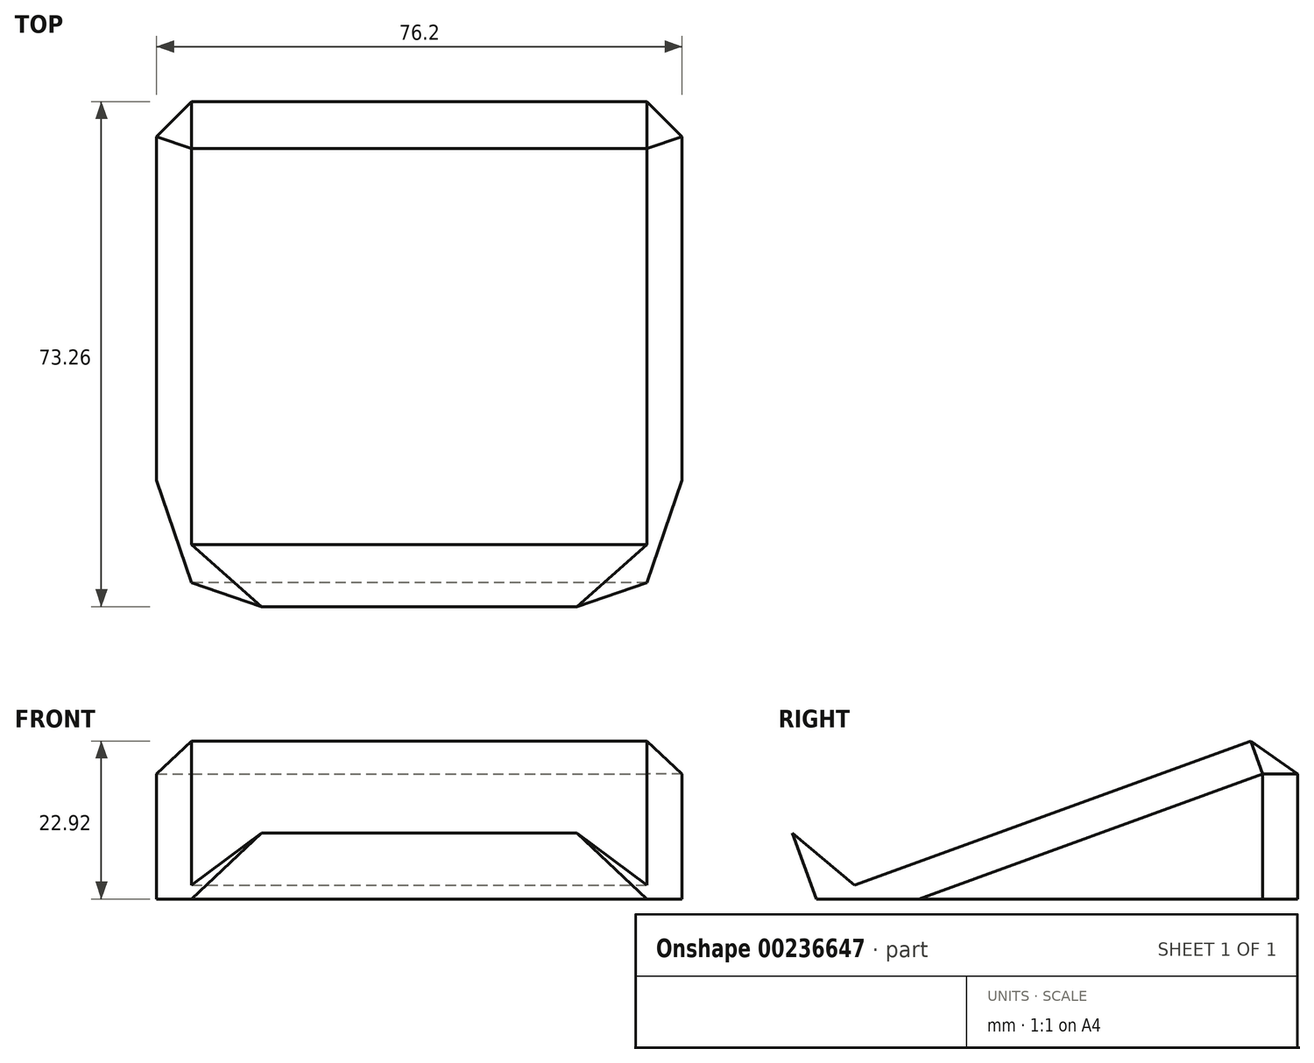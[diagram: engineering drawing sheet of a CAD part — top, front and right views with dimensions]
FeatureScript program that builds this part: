
annotation { "Feature Type Name" : "Feature", "Feature Type Description" : "" }
export const myFeature = defineFeature(function(context is Context, id is Id, definition is map)
    precondition{}
    {
        {
            var Q0;
            Q0=qCreatedBy(makeId("Right.planeOp"),FACE);
            var sketch = newSketch(context, id + "F0", { "sketchPlane" : qUnion([Q0])});
            skLineSegment(sketch, "E0", {"start": v(0, 0) * mm, "end": v(0, 25.4) * mm});
            skLineSegment(sketch, "E1", {"start": v(0, 0) * mm, "end": v(-69.79, 0) * mm});
            skLineSegment(sketch, "E2", {"start": v(-69.79, 0) * mm, "end": v(0, 25.4) * mm});
            skSolve(sketch);
        }
        {
            var Q0;
            Q0 = qSketchRegion(id + "F0", true);
            extrude(context, id + "F1", {"entities" : qUnion([Q0]), "depth" : 76.2 * mm});
        }
        {
            var Q0;
            Q0=makeQuery(id+"F1.opExtrude","CAP_EDGE",EDGE,{"disambiguationData":[OSD([sQuery(id+"F0.wireOp",EDGE,"E2")])],"isStart":true});
            var Q1;
            Q1=makeQuery(id+"F1.opExtrude","CAP_EDGE",EDGE,{"disambiguationData":[OSD([sQuery(id+"F0.wireOp",EDGE,"E0")])],"isStart":true});
            var Q2;
            Q2=makeQuery(id+"F1.opExtrude","SWEPT_EDGE",EDGE,{"disambiguationData":[OSD([sQuery(id+"F0.wireOp",EDGE,"E0"),sQuery(id+"F0.wireOp",EDGE,"E2")])]});
            var Q3;
            Q3=makeQuery(id+"F1.opExtrude","CAP_EDGE",EDGE,{"disambiguationData":[OSD([sQuery(id+"F0.wireOp",EDGE,"E2")])],"isStart":false});
            var Q4;
            Q4=makeQuery(id+"F1.opExtrude","CAP_EDGE",EDGE,{"disambiguationData":[OSD([sQuery(id+"F0.wireOp",EDGE,"E0")])],"isStart":false});
            chamfer(context, id + "F2", {"entities" : qUnion([Q0, Q1, Q2, Q3, Q4]), "width" : 5.08 * mm, "tangentPropagation" : true});
        }
        {
            var Q0;
            Q0=makeQuery(id+"F1.opExtrude","SWEPT_FACE",FACE,{"disambiguationData":[OSD([sQuery(id+"F0.wireOp",EDGE,"E2")])]});
            var sketch = newSketch(context, id + "F3", { "sketchPlane" : qUnion([Q0])});
            skLineSegment(sketch, "E3.bottom", {"start": v(71.12, -65.58) * mm, "end": v(5.08, -65.58) * mm});
            skLineSegment(sketch, "E3.top", {"start": v(71.12, -59.23) * mm, "end": v(5.08, -59.23) * mm});
            skLineSegment(sketch, "E3.left", {"start": v(71.12, -65.58) * mm, "end": v(71.12, -59.23) * mm});
            skLineSegment(sketch, "E3.right", {"start": v(5.08, -65.58) * mm, "end": v(5.08, -59.23) * mm});
            skSolve(sketch);
        }
        {
            var Q0;
            Q0 = qSketchRegion(id + "F3", true);
            extrude(context, id + "F4", {"entities" : qUnion([Q0]), "operationType" : NewBodyOperationType.ADD, "depth" : 10.16 * mm});
        }
        {
            var Q0;
            Q0=makeQuery(id+"F4.opExtrude","CAP_EDGE",EDGE,{"disambiguationData":[OSD([sQuery(id+"F3.wireOp",EDGE,"E3.right")])],"isStart":false});
            var Q1;
            Q1=makeQuery(id+"F4.opExtrude","CAP_EDGE",EDGE,{"disambiguationData":[OSD([sQuery(id+"F3.wireOp",EDGE,"E3.left")])],"isStart":false});
            chamfer(context, id + "F5", {"entities" : qUnion([Q0, Q1]), "width" : 10.16 * mm, "tangentPropagation" : true});
        }
        {
            var Q0;
            Q0=makeQuery(id+"F4.opExtrude","CAP_EDGE",EDGE,{"disambiguationData":[OSD([sQuery(id+"F3.wireOp",EDGE,"E3.top")])],"isStart":false});
            chamfer(context, id + "F6", {"entities" : qUnion([Q0]), "chamferType" : ChamferType.OFFSET_ANGLE, "width" : 6.35 * mm, "oppositeDirection" : false, "angle" : 60 * degree, "tangentPropagation" : true});
        }
    });
